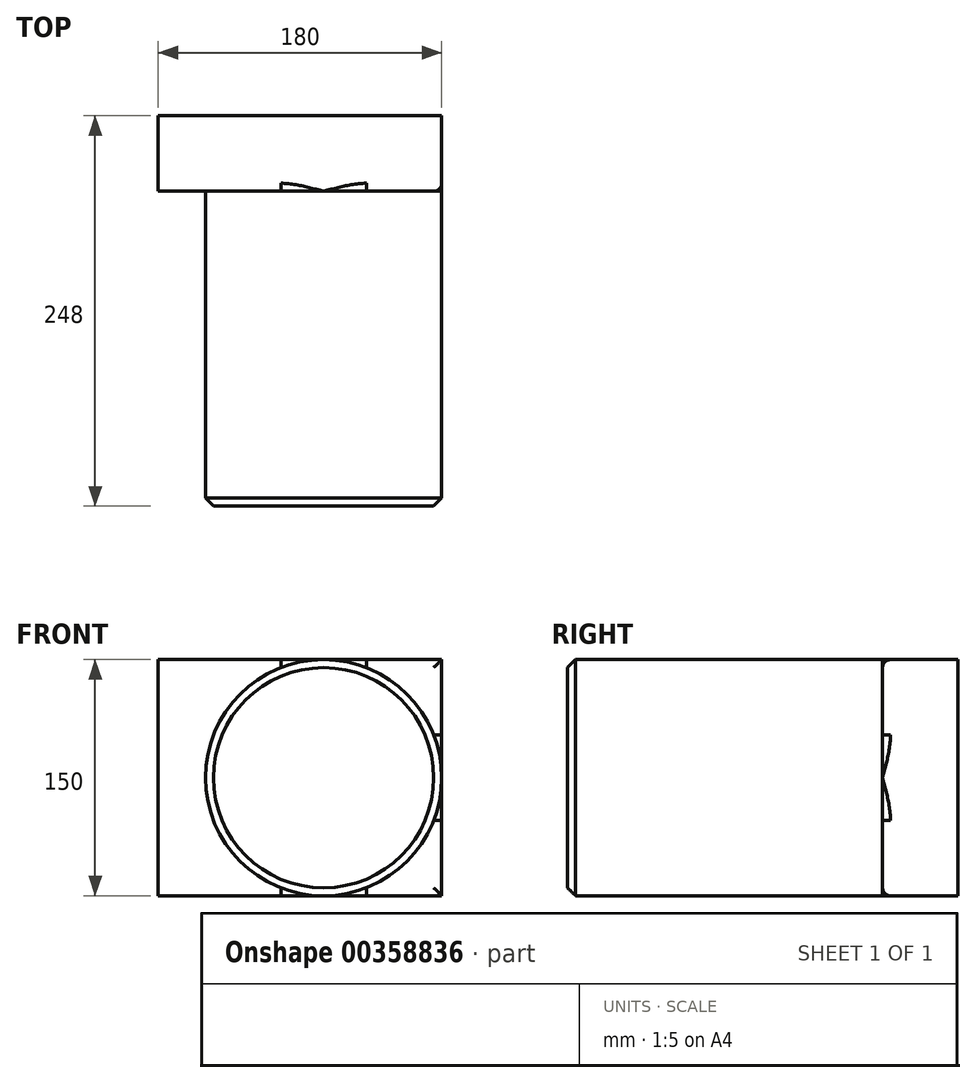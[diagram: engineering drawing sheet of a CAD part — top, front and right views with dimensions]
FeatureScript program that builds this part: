
annotation { "Feature Type Name" : "Feature", "Feature Type Description" : "" }
export const myFeature = defineFeature(function(context is Context, id is Id, definition is map)
    precondition{}
    {
        {
            var Q0;
            Q0=qCreatedBy(makeId("Front.planeOp"),FACE);
            var sketch = newSketch(context, id + "F0", { "sketchPlane" : qUnion([Q0])});
            skLineSegment(sketch, "E0.bottom", {"start": v(90, 75) * mm, "end": v(-90, 75) * mm});
            skLineSegment(sketch, "E0.top", {"start": v(90, -75) * mm, "end": v(-90, -75) * mm});
            skLineSegment(sketch, "E0.left", {"start": v(90, 75) * mm, "end": v(90, -75) * mm});
            skLineSegment(sketch, "E0.right", {"start": v(-90, 75) * mm, "end": v(-90, -75) * mm});
            skPoint(sketch, "E0.middle", {"position": v(0, 0) * mm});
            skSolve(sketch);
        }
        {
            var Q0;
            Q0 = qSketchRegion(id + "F0", true);
            extrude(context, id + "F1", {"entities" : qUnion([Q0]), "depth" : 48 * mm});
        }
        {
            var Q0;
            Q0=makeQuery(id+"F1.opExtrude","CAP_FACE",FACE,{"disambiguationData":[OSD([sQuery(id+"F0.wireOp",EDGE,"E0.bottom"),sQuery(id+"F0.wireOp",EDGE,"E0.top"),sQuery(id+"F0.wireOp",EDGE,"E0.left"),sQuery(id+"F0.wireOp",EDGE,"E0.right")])],"isStart":false});
            var sketch = newSketch(context, id + "F2", { "sketchPlane" : qUnion([Q0])});
            skCircle(sketch, "E1", {"center": v(15, 0) * mm, "radius": 75 * mm});
            skSolve(sketch);
        }
        {
            var Q0;
            {var subQ0=sQuery(id+"F2.wireOp",EDGE,"E1");var subQ1=makeQuery(id+"F2.imprint","INTERSECT",VERTEX,{"derivedFrom":[makeQuery(id+"F1.opExtrude","CAP_EDGE",EDGE,{"disambiguationData":[OSD([sQuery(id+"F0.wireOp",EDGE,"E0.bottom")])],"isStart":false}),subQ0]});Q0=makeQuery(id+"F2.imprint","IMPRINT",FACE,{"disambiguationData":[TD([[makeQuery(id+"F2.imprint","IMPRINT",EDGE,{"disambiguationData":[TD([[subQ1,1.0]])],"derivedFrom":subQ0}),1.0]])]});}
            extrude(context, id + "F3", {"entities" : qUnion([Q0]), "operationType" : NewBodyOperationType.ADD, "depth" : 200 * mm});
        }
        {
            var Q0;
            {var subQ0=sQuery(id+"F0.wireOp",EDGE,"E0.bottom");var subQ1=sQuery(id+"F0.wireOp",EDGE,"E0.left");Q0=makeQuery(id+"F3.boolean.opBoolean","SPLIT",EDGE,{"disambiguationData":[TD([makeQuery(id+"F1.opExtrude","SWEPT_FACE",FACE,{"disambiguationData":[OSD([subQ0])]})])],"derivedFrom":makeQuery(id+"F1.opExtrude","CAP_EDGE",EDGE,{"disambiguationData":[OSD([subQ1])],"isStart":false})});}
            var Q1;
            {var subQ0=sQuery(id+"F0.wireOp",EDGE,"E0.bottom");var subQ1=sQuery(id+"F0.wireOp",EDGE,"E0.left");Q1=makeQuery(id+"F3.boolean.opBoolean","SPLIT",EDGE,{"disambiguationData":[TD([makeQuery(id+"F1.opExtrude","SWEPT_FACE",FACE,{"disambiguationData":[OSD([subQ1])]})])],"derivedFrom":makeQuery(id+"F1.opExtrude","CAP_EDGE",EDGE,{"disambiguationData":[OSD([subQ0])],"isStart":false})});}
            var Q2;
            {var subQ0=sQuery(id+"F0.wireOp",EDGE,"E0.left");var subQ1=sQuery(id+"F0.wireOp",EDGE,"E0.top");Q2=makeQuery(id+"F3.boolean.opBoolean","SPLIT",EDGE,{"disambiguationData":[TD([makeQuery(id+"F1.opExtrude","SWEPT_FACE",FACE,{"disambiguationData":[OSD([subQ0])]})])],"derivedFrom":makeQuery(id+"F1.opExtrude","CAP_EDGE",EDGE,{"disambiguationData":[OSD([subQ1])],"isStart":false})});}
            fillet(context, id + "F4", {"entities" : qUnion([Q0, Q1, Q2]), "radius" : 5.08 * mm, "tangentPropagation" : true, "allowEdgeOverflow" : false});
        }
        {
            var Q0;
            Q0=makeQuery(id+"F3.opExtrude","CAP_FACE",FACE,{"disambiguationData":[OSD([sQuery(id+"F2.wireOp",EDGE,"E1")])],"isStart":false});
            chamfer(context, id + "F5", {"entities" : qUnion([Q0]), "width" : 5.08 * mm, "tangentPropagation" : true});
        }
    });
